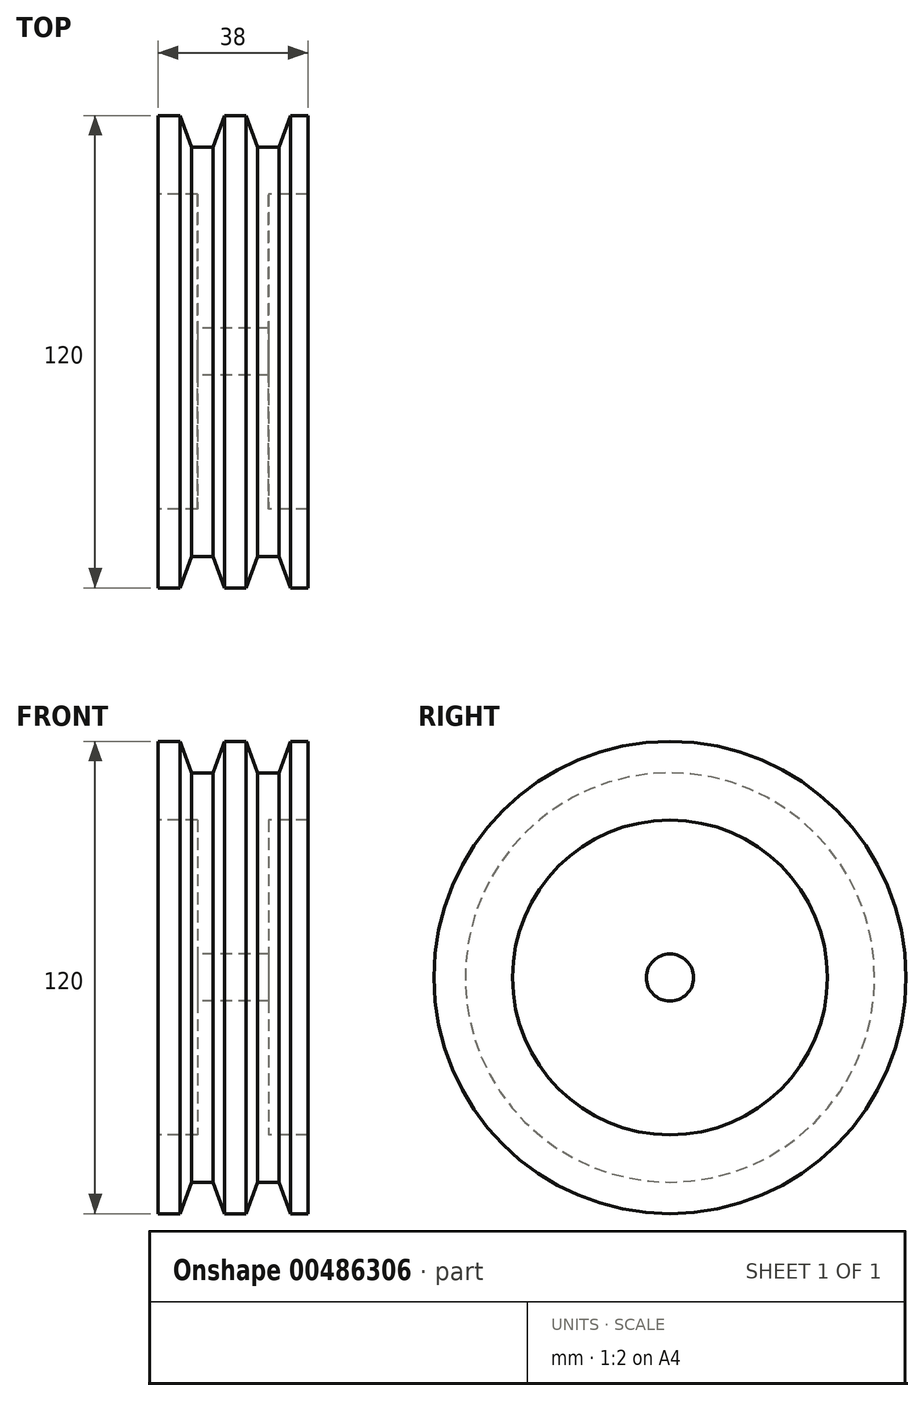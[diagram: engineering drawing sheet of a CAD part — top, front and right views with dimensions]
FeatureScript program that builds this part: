
annotation { "Feature Type Name" : "Feature", "Feature Type Description" : "" }
export const myFeature = defineFeature(function(context is Context, id is Id, definition is map)
    precondition{}
    {
        {
            var Q0;
            Q0=qCreatedBy(makeId("Front.planeOp"),FACE);
            var sketch = newSketch(context, id + "F0", { "sketchPlane" : qUnion([Q0])});
            skLineSegment(sketch, "E0", {"start": v(-15.24, 6) * mm, "end": v(-15.24, 40) * mm});
            skLineSegment(sketch, "E1", {"start": v(-15.24, 40) * mm, "end": v(-25.24, 40) * mm});
            skLineSegment(sketch, "E2", {"start": v(-25.24, 40) * mm, "end": v(-25.24, 60) * mm});
            skLineSegment(sketch, "E3", {"start": v(-25.24, 60) * mm, "end": v(-19.74, 60) * mm});
            skLineSegment(sketch, "E4", {"start": v(-19.74, 60) * mm, "end": v(-16.82, 52) * mm});
            skLineSegment(sketch, "E5", {"start": v(-16.82, 52) * mm, "end": v(-11.32, 52) * mm});
            skLineSegment(sketch, "E6", {"start": v(-11.32, 52) * mm, "end": v(-8.41, 60) * mm});
            skLineSegment(sketch, "E7", {"start": v(-8.41, 60) * mm, "end": v(-2.91, 60) * mm});
            skLineSegment(sketch, "E8", {"start": v(-2.91, 60) * mm, "end": v(0, 52) * mm});
            skLineSegment(sketch, "E9", {"start": v(0, 52) * mm, "end": v(5.5, 52) * mm});
            skLineSegment(sketch, "E10", {"start": v(5.5, 52) * mm, "end": v(8.41, 60) * mm});
            skLineSegment(sketch, "E11", {"start": v(8.41, 60) * mm, "end": v(12.76, 60) * mm});
            skLineSegment(sketch, "E12", {"start": v(12.76, 60) * mm, "end": v(12.76, 40) * mm});
            skLineSegment(sketch, "E13", {"start": v(12.76, 40) * mm, "end": v(2.76, 40) * mm});
            skLineSegment(sketch, "E14", {"start": v(2.76, 40) * mm, "end": v(2.76, 6) * mm});
            skLineSegment(sketch, "E15", {"start": v(2.76, 6) * mm, "end": v(-15.24, 6) * mm});
            skLineSegment(sketch, "E16", {"start": v(-72.37, 0) * mm, "end": v(96.1, 0) * mm});
            skSolve(sketch);
        }
        {
            var Q0;
            Q0=makeQuery(id+"F0.imprint","IMPRINT",FACE,{"disambiguationData":[TD([[makeQuery(id+"F0.imprint","IMPRINT",EDGE,{"derivedFrom":sQuery(id+"F0.wireOp",EDGE,"E0")}),-1.0]])]});
            var Q1;
            Q1=sQuery(id+"F0.wireOp",EDGE,"E16");
            revolve(context, id + "F1", {"surfaceOperationType" : NewSurfaceOperationType.NEW, "entities" : qUnion([Q0]), "axis" : qUnion([Q1]), "revolveType" : RevolveType.FULL});
        }
    });
